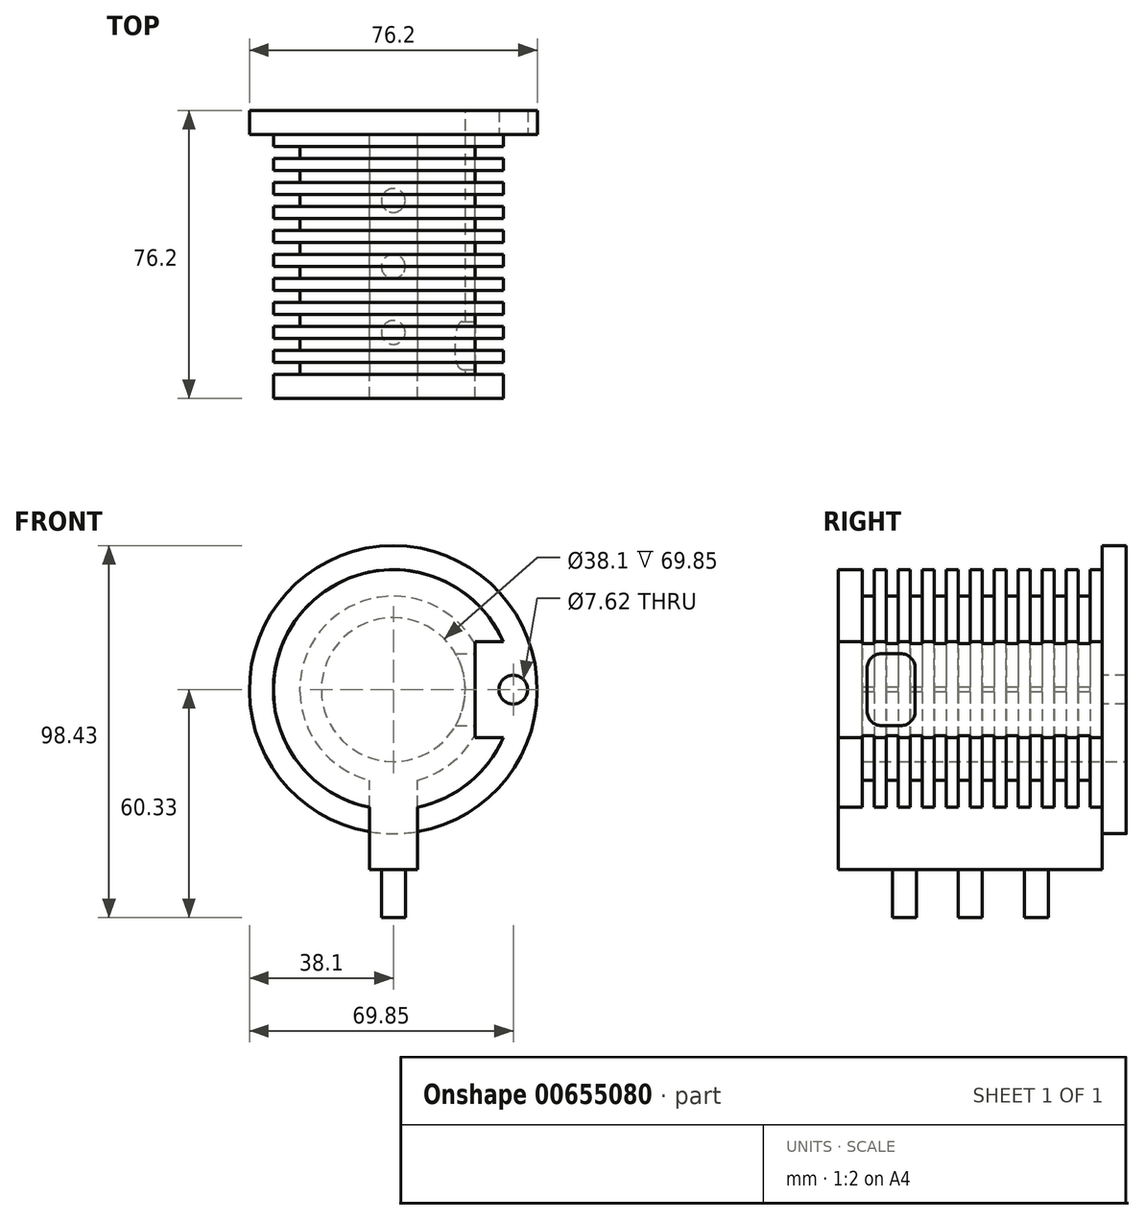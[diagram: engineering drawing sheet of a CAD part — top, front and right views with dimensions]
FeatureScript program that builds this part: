
annotation { "Feature Type Name" : "Feature", "Feature Type Description" : "" }
export const myFeature = defineFeature(function(context is Context, id is Id, definition is map)
    precondition{}
    {
        {
            var Q0;
            Q0=qCreatedBy(makeId("Right.planeOp"),FACE);
            cPlane(context, id + "F0", {"entities" : qUnion([Q0]), "cplaneType" : CPlaneType.OFFSET, "offset" : 31.75 * mm, "oppositeDirection" : true, "width" : 152.4 * mm, "height" : 152.4 * mm});
        }
        {
            var Q0;
            Q0=qCreatedBy(makeId("Front.planeOp"),FACE);
            var sketch = newSketch(context, id + "F1", { "sketchPlane" : qUnion([Q0])});
            skCircle(sketch, "E0", {"center": v(0, 0) * mm, "radius": 19.05 * mm});
            skCircle(sketch, "E1", {"center": v(0, 0) * mm, "radius": 31.75 * mm});
            skSolve(sketch);
        }
        {
            var Q0;
            Q0 = qSketchRegion(id + "F1", true);
            extrude(context, id + "F2", {"entities" : qUnion([Q0]), "depth" : 25.4 * mm, "offsetDistance" : 25.4 * mm, "hasSecondDirection" : true, "secondDirectionOppositeDirection" : true, "secondDirectionDepth" : 38.1 * mm});
        }
        {
            var Q0;
            Q0=qCreatedBy(makeId("Front.planeOp"),FACE);
            var sketch = newSketch(context, id + "F3", { "sketchPlane" : qUnion([Q0])});
            skLineSegment(sketch, "E2.bottom", {"start": v(21.59, 12.7) * mm, "end": v(31.75, 12.7) * mm});
            skLineSegment(sketch, "E2.top", {"start": v(21.59, -12.7) * mm, "end": v(31.75, -12.7) * mm});
            skLineSegment(sketch, "E2.left", {"start": v(21.59, 12.7) * mm, "end": v(21.59, -12.7) * mm});
            skLineSegment(sketch, "E2.right", {"start": v(31.75, 12.7) * mm, "end": v(31.75, -12.7) * mm});
            skSolve(sketch);
        }
        {
            var Q0;
            Q0 = qSketchRegion(id + "F3", true);
            extrude(context, id + "F4", {"entities" : qUnion([Q0]), "operationType" : NewBodyOperationType.REMOVE, "depth" : 25.4 * mm, "offsetDistance" : 25.4 * mm, "hasSecondDirection" : true, "secondDirectionOppositeDirection" : true, "secondDirectionDepth" : 38.1 * mm});
        }
        {
            var Q0;
            Q0 = qSketchRegion(id + "F3", true);
            extrude(context, id + "F5", {"entities" : qUnion([Q0]), "operationType" : NewBodyOperationType.REMOVE, "oppositeDirection" : true, "depth" : 25.4 * mm, "offsetDistance" : 25.4 * mm, "hasSecondDirection" : true, "secondDirectionOppositeDirection" : false, "secondDirectionDepth" : 25.4 * mm});
        }
        {
            var Q0;
            Q0=makeQuery(id+"F4.boolean.opBoolean","COPY",FACE,{"derivedFrom":makeQuery(id+"F4.opExtrude","SWEPT_FACE",FACE,{"disambiguationData":[OSD([sQuery(id+"F3.wireOp",EDGE,"E2.left")])]})});
            var sketch = newSketch(context, id + "F6", { "sketchPlane" : qUnion([Q0])});
            skLineSegment(sketch, "E3.bottom", {"start": v(-20.32, 9.52) * mm, "end": v(-15.24, 9.52) * mm});
            skLineSegment(sketch, "E3.top", {"start": v(-20.32, -9.53) * mm, "end": v(-15.24, -9.53) * mm});
            skLineSegment(sketch, "E3.left", {"start": v(-24.13, 5.71) * mm, "end": v(-24.13, -5.72) * mm});
            skLineSegment(sketch, "E3.right", {"start": v(-11.43, 5.71) * mm, "end": v(-11.43, -5.72) * mm});
            skPoint(sketch, "E4.visualSharp", {"position": v(-24.13, 9.52) * mm});
            skArc(sketch, "E4.filletArc", {"start": v(-20.32, 9.52) * mm, "mid": v(-23.01, 8.4) * mm, "end": v(-24.13, 5.71) * mm});
            skPoint(sketch, "E5.visualSharp", {"position": v(-11.43, 9.53) * mm});
            skArc(sketch, "E5.filletArc", {"start": v(-11.43, 5.71) * mm, "mid": v(-12.55, 8.4) * mm, "end": v(-15.24, 9.52) * mm});
            skPoint(sketch, "E6.visualSharp", {"position": v(-24.13, -9.53) * mm});
            skArc(sketch, "E6.filletArc", {"start": v(-24.13, -5.72) * mm, "mid": v(-23.01, -8.4) * mm, "end": v(-20.32, -9.53) * mm});
            skPoint(sketch, "E7.visualSharp", {"position": v(-11.43, -9.53) * mm});
            skArc(sketch, "E7.filletArc", {"start": v(-15.24, -9.53) * mm, "mid": v(-12.55, -8.4) * mm, "end": v(-11.43, -5.72) * mm});
            skSolve(sketch);
        }
        {
            var Q0;
            Q0 = qSketchRegion(id + "F6", true);
            extrude(context, id + "F7", {"entities" : qUnion([Q0]), "operationType" : NewBodyOperationType.REMOVE, "endBound" : BoundingType.UP_TO_NEXT, "oppositeDirection" : true, "depth" : 25.4 * mm, "offsetDistance" : 25.4 * mm});
        }
        {
            var Q0;
            Q0=makeQuery(id+"F2.opExtrude","CAP_FACE",FACE,{"disambiguationData":[OSD([sQuery(id+"F1.wireOp",EDGE,"E0"),sQuery(id+"F1.wireOp",EDGE,"E1")])],"isStart":false});
            var sketch = newSketch(context, id + "F8", { "sketchPlane" : qUnion([Q0])});
            skArc(sketch, "E8", {"start": v(29.1, 12.7) * mm, "mid": v(-31.75, 0) * mm, "end": v(29.1, -12.7) * mm});
            skLineSegment(sketch, "E9", {"start": v(29.1, 12.7) * mm, "end": v(21.59, 12.7) * mm});
            skLineSegment(sketch, "E10", {"start": v(21.59, 12.7) * mm, "end": v(21.59, -12.7) * mm});
            skLineSegment(sketch, "E11", {"start": v(21.59, -12.7) * mm, "end": v(29.1, -12.7) * mm});
            skSolve(sketch);
        }
        {
            var Q0;
            Q0 = qSketchRegion(id + "F8", true);
            extrude(context, id + "F9", {"entities" : qUnion([Q0]), "operationType" : NewBodyOperationType.ADD, "depth" : 6.35 * mm, "offsetDistance" : 25.4 * mm});
        }
        {
            var Q0;
            Q0=qCreatedBy(id+"F0.planeOp",FACE);
            var sketch = newSketch(context, id + "F10", { "sketchPlane" : qUnion([Q0])});
            skLineSegment(sketch, "E12.bottom", {"start": v(34.93, -0.63) * mm, "end": v(31.75, -0.63) * mm});
            skLineSegment(sketch, "E12.top", {"start": v(34.93, 0.64) * mm, "end": v(31.75, 0.64) * mm});
            skLineSegment(sketch, "E12.left", {"start": v(34.93, -0.63) * mm, "end": v(34.93, 0.64) * mm});
            skLineSegment(sketch, "E12.right", {"start": v(31.75, -0.63) * mm, "end": v(31.75, 0.64) * mm});
            skLineSegment(sketch, "E13.1.0.0", {"start": v(28.58, -0.63) * mm, "end": v(28.58, 0.64) * mm});
            skLineSegment(sketch, "E13.1.0.1", {"start": v(28.58, 0.64) * mm, "end": v(25.4, 0.64) * mm});
            skLineSegment(sketch, "E13.1.0.2", {"start": v(28.58, -0.63) * mm, "end": v(25.4, -0.63) * mm});
            skLineSegment(sketch, "E13.1.0.3", {"start": v(25.4, -0.63) * mm, "end": v(25.4, 0.64) * mm});
            skLineSegment(sketch, "E13.2.0.0", {"start": v(22.23, -0.63) * mm, "end": v(22.23, 0.64) * mm});
            skLineSegment(sketch, "E13.2.0.1", {"start": v(22.23, 0.64) * mm, "end": v(19.05, 0.64) * mm});
            skLineSegment(sketch, "E13.2.0.2", {"start": v(22.23, -0.63) * mm, "end": v(19.05, -0.63) * mm});
            skLineSegment(sketch, "E13.2.0.3", {"start": v(19.05, -0.63) * mm, "end": v(19.05, 0.64) * mm});
            skLineSegment(sketch, "E13.3.0.0", {"start": v(15.88, -0.63) * mm, "end": v(15.88, 0.64) * mm});
            skLineSegment(sketch, "E13.3.0.1", {"start": v(15.88, 0.64) * mm, "end": v(12.7, 0.64) * mm});
            skLineSegment(sketch, "E13.3.0.2", {"start": v(15.88, -0.63) * mm, "end": v(12.7, -0.63) * mm});
            skLineSegment(sketch, "E13.3.0.3", {"start": v(12.7, -0.63) * mm, "end": v(12.7, 0.64) * mm});
            skLineSegment(sketch, "E13.4.0.0", {"start": v(9.52, -0.63) * mm, "end": v(9.52, 0.64) * mm});
            skLineSegment(sketch, "E13.4.0.1", {"start": v(9.52, 0.64) * mm, "end": v(6.35, 0.64) * mm});
            skLineSegment(sketch, "E13.4.0.2", {"start": v(9.52, -0.63) * mm, "end": v(6.35, -0.63) * mm});
            skLineSegment(sketch, "E13.4.0.3", {"start": v(6.35, -0.63) * mm, "end": v(6.35, 0.64) * mm});
            skLineSegment(sketch, "E13.5.0.0", {"start": v(3.17, -0.63) * mm, "end": v(3.17, 0.64) * mm});
            skLineSegment(sketch, "E13.5.0.1", {"start": v(3.17, 0.64) * mm, "end": v(0, 0.64) * mm});
            skLineSegment(sketch, "E13.5.0.2", {"start": v(3.17, -0.63) * mm, "end": v(0, -0.63) * mm});
            skLineSegment(sketch, "E13.5.0.3", {"start": v(0, -0.63) * mm, "end": v(0, 0.64) * mm});
            skLineSegment(sketch, "E13.6.0.0", {"start": v(-3.18, -0.63) * mm, "end": v(-3.18, 0.64) * mm});
            skLineSegment(sketch, "E13.6.0.1", {"start": v(-3.18, 0.64) * mm, "end": v(-6.35, 0.64) * mm});
            skLineSegment(sketch, "E13.6.0.2", {"start": v(-3.18, -0.63) * mm, "end": v(-6.35, -0.63) * mm});
            skLineSegment(sketch, "E13.6.0.3", {"start": v(-6.35, -0.63) * mm, "end": v(-6.35, 0.64) * mm});
            skLineSegment(sketch, "E13.7.0.0", {"start": v(-9.53, -0.63) * mm, "end": v(-9.53, 0.64) * mm});
            skLineSegment(sketch, "E13.7.0.1", {"start": v(-9.53, 0.64) * mm, "end": v(-12.7, 0.64) * mm});
            skLineSegment(sketch, "E13.7.0.2", {"start": v(-9.53, -0.63) * mm, "end": v(-12.7, -0.63) * mm});
            skLineSegment(sketch, "E13.7.0.3", {"start": v(-12.7, -0.63) * mm, "end": v(-12.7, 0.64) * mm});
            skLineSegment(sketch, "E13.8.0.0", {"start": v(-15.88, -0.63) * mm, "end": v(-15.88, 0.64) * mm});
            skLineSegment(sketch, "E13.8.0.1", {"start": v(-15.88, 0.64) * mm, "end": v(-19.05, 0.64) * mm});
            skLineSegment(sketch, "E13.8.0.2", {"start": v(-15.88, -0.63) * mm, "end": v(-19.05, -0.63) * mm});
            skLineSegment(sketch, "E13.8.0.3", {"start": v(-19.05, -0.63) * mm, "end": v(-19.05, 0.64) * mm});
            skLineSegment(sketch, "E13.9.0.0", {"start": v(-22.23, -0.63) * mm, "end": v(-22.23, 0.64) * mm});
            skLineSegment(sketch, "E13.9.0.1", {"start": v(-22.23, 0.64) * mm, "end": v(-25.4, 0.64) * mm});
            skLineSegment(sketch, "E13.9.0.2", {"start": v(-22.23, -0.63) * mm, "end": v(-25.4, -0.63) * mm});
            skLineSegment(sketch, "E13.9.0.3", {"start": v(-25.4, -0.63) * mm, "end": v(-25.4, 0.64) * mm});
            skLineSegment(sketch, "E13.direction1", {"start": v(32.39, -0.63) * mm, "end": v(26.04, -0.63) * mm, "construction": true});
            skSolve(sketch);
        }
        {
            var Q0;
            Q0 = qSketchRegion(id + "F10", true);
            extrude(context, id + "F11", {"entities" : qUnion([Q0]), "operationType" : NewBodyOperationType.REMOVE, "depth" : 7 * mm, "offsetDistance" : 25.4 * mm});
        }
        {
            var Q0;
            Q0=makeQuery(id+"F11.boolean.opBoolean","COPY",FACE,{"derivedFrom":makeQuery(id+"F11.opExtrude","SWEPT_FACE",FACE,{"disambiguationData":[OSD([sQuery(id+"F10.wireOp",EDGE,"E12.top")])]})});
            var Q1;
            Q1=makeQuery(id+"F11.boolean.opBoolean","COPY",FACE,{"derivedFrom":makeQuery(id+"F11.opExtrude","SWEPT_FACE",FACE,{"disambiguationData":[OSD([sQuery(id+"F10.wireOp",EDGE,"E13.1.0.1")])]})});
            var Q2;
            Q2=makeQuery(id+"F11.boolean.opBoolean","COPY",FACE,{"derivedFrom":makeQuery(id+"F11.opExtrude","SWEPT_FACE",FACE,{"disambiguationData":[OSD([sQuery(id+"F10.wireOp",EDGE,"E13.2.0.1")])]})});
            var Q3;
            Q3=makeQuery(id+"F11.boolean.opBoolean","COPY",FACE,{"derivedFrom":makeQuery(id+"F11.opExtrude","SWEPT_FACE",FACE,{"disambiguationData":[OSD([sQuery(id+"F10.wireOp",EDGE,"E13.3.0.1")])]})});
            var Q4;
            Q4=makeQuery(id+"F11.boolean.opBoolean","COPY",FACE,{"derivedFrom":makeQuery(id+"F11.opExtrude","SWEPT_FACE",FACE,{"disambiguationData":[OSD([sQuery(id+"F10.wireOp",EDGE,"E13.4.0.1")])]})});
            var Q5;
            Q5=makeQuery(id+"F11.boolean.opBoolean","COPY",FACE,{"derivedFrom":makeQuery(id+"F11.opExtrude","SWEPT_FACE",FACE,{"disambiguationData":[OSD([sQuery(id+"F10.wireOp",EDGE,"E13.5.0.1")])]})});
            var Q6;
            Q6=makeQuery(id+"F11.boolean.opBoolean","COPY",FACE,{"derivedFrom":makeQuery(id+"F11.opExtrude","SWEPT_FACE",FACE,{"disambiguationData":[OSD([sQuery(id+"F10.wireOp",EDGE,"E13.6.0.1")])]})});
            var Q7;
            Q7=makeQuery(id+"F11.boolean.opBoolean","COPY",FACE,{"derivedFrom":makeQuery(id+"F11.opExtrude","SWEPT_FACE",FACE,{"disambiguationData":[OSD([sQuery(id+"F10.wireOp",EDGE,"E13.7.0.1")])]})});
            var Q8;
            Q8=makeQuery(id+"F11.boolean.opBoolean","COPY",FACE,{"derivedFrom":makeQuery(id+"F11.opExtrude","SWEPT_FACE",FACE,{"disambiguationData":[OSD([sQuery(id+"F10.wireOp",EDGE,"E13.8.0.1")])]})});
            var Q9;
            Q9=makeQuery(id+"F11.boolean.opBoolean","COPY",FACE,{"derivedFrom":makeQuery(id+"F11.opExtrude","SWEPT_FACE",FACE,{"disambiguationData":[OSD([sQuery(id+"F10.wireOp",EDGE,"E13.9.0.1")])]})});
            var Q10;
            Q10=makeQuery(id+"F2.opExtrude","CAP_EDGE",EDGE,{"disambiguationData":[OSD([sQuery(id+"F1.wireOp",EDGE,"E0")])],"isStart":true});
            revolve(context, id + "F12", {"operationType" : NewBodyOperationType.REMOVE, "entities" : qUnion([Q0, Q1, Q2, Q3, Q4, Q5, Q6, Q7, Q8, Q9]), "axis" : qUnion([Q10]), "revolveType" : RevolveType.FULL, "oppositeDirection" : true});
        }
        {
            var Q0;
            Q0=qCreatedBy(makeId("Top.planeOp"),FACE);
            cPlane(context, id + "F13", {"entities" : qUnion([Q0]), "cplaneType" : CPlaneType.OFFSET, "offset" : 19.05 * mm, "oppositeDirection" : true, "width" : 152.4 * mm, "height" : 152.4 * mm});
        }
        {
            var Q0;
            Q0=qCreatedBy(id+"F13.planeOp",FACE);
            var sketch = newSketch(context, id + "F14", { "sketchPlane" : qUnion([Q0])});
            skLineSegment(sketch, "E14.bottom", {"start": v(-6.35, -31.75) * mm, "end": v(6.35, -31.75) * mm});
            skLineSegment(sketch, "E14.top", {"start": v(-6.35, 38.1) * mm, "end": v(6.35, 38.1) * mm});
            skLineSegment(sketch, "E14.left", {"start": v(-6.35, -31.75) * mm, "end": v(-6.35, 38.1) * mm});
            skLineSegment(sketch, "E14.right", {"start": v(6.35, -31.75) * mm, "end": v(6.35, 38.1) * mm});
            skSolve(sketch);
        }
        {
            var Q0;
            Q0 = qSketchRegion(id + "F14", true);
            extrude(context, id + "F15", {"entities" : qUnion([Q0]), "operationType" : NewBodyOperationType.ADD, "oppositeDirection" : true, "depth" : 28.57 * mm, "offsetDistance" : 25.4 * mm});
        }
        {
            var Q0;
            Q0=makeQuery(id+"F15.opExtrude","CAP_FACE",FACE,{"disambiguationData":[OSD([sQuery(id+"F14.wireOp",EDGE,"E14.bottom"),sQuery(id+"F14.wireOp",EDGE,"E14.top"),sQuery(id+"F14.wireOp",EDGE,"E14.left"),sQuery(id+"F14.wireOp",EDGE,"E14.right")])],"isStart":false});
            var sketch = newSketch(context, id + "F16", { "sketchPlane" : qUnion([Q0])});
            skCircle(sketch, "E15", {"center": v(0, 14.29) * mm, "radius": 3.18 * mm});
            skCircle(sketch, "E16", {"center": v(0, -20.64) * mm, "radius": 3.18 * mm});
            skCircle(sketch, "E17", {"center": v(0, -3.18) * mm, "radius": 3.18 * mm});
            skSolve(sketch);
        }
        {
            var Q0;
            Q0 = qSketchRegion(id + "F16", true);
            extrude(context, id + "F17", {"entities" : qUnion([Q0]), "operationType" : NewBodyOperationType.ADD, "depth" : 12.7 * mm, "offsetDistance" : 25.4 * mm});
        }
        {
            var Q0;
            Q0=makeQuery(id+"F15.boolean.opBoolean","MERGE",FACE,{"derivedFrom":[makeQuery(id+"F2.opExtrude","CAP_FACE",FACE,{"disambiguationData":[OSD([sQuery(id+"F1.wireOp",EDGE,"E0"),sQuery(id+"F1.wireOp",EDGE,"E1")])],"isStart":true}),makeQuery(id+"F15.opExtrude","SWEPT_FACE",FACE,{"disambiguationData":[OSD([sQuery(id+"F14.wireOp",EDGE,"E14.top")])]})]});
            var sketch = newSketch(context, id + "F18", { "sketchPlane" : qUnion([Q0])});
            skCircle(sketch, "E18", {"center": v(0, 0) * mm, "radius": 38.1 * mm});
            skCircle(sketch, "E19", {"center": v(0, 0) * mm, "radius": 19.05 * mm});
            skCircle(sketch, "E20", {"center": v(-31.75, 0) * mm, "radius": 3.81 * mm});
            skSolve(sketch);
        }
        {
            var Q0;
            Q0 = qSketchRegion(id + "F18", true);
            extrude(context, id + "F19", {"entities" : qUnion([Q0]), "operationType" : NewBodyOperationType.ADD, "depth" : 6.35 * mm, "offsetDistance" : 25.4 * mm});
        }
    });
